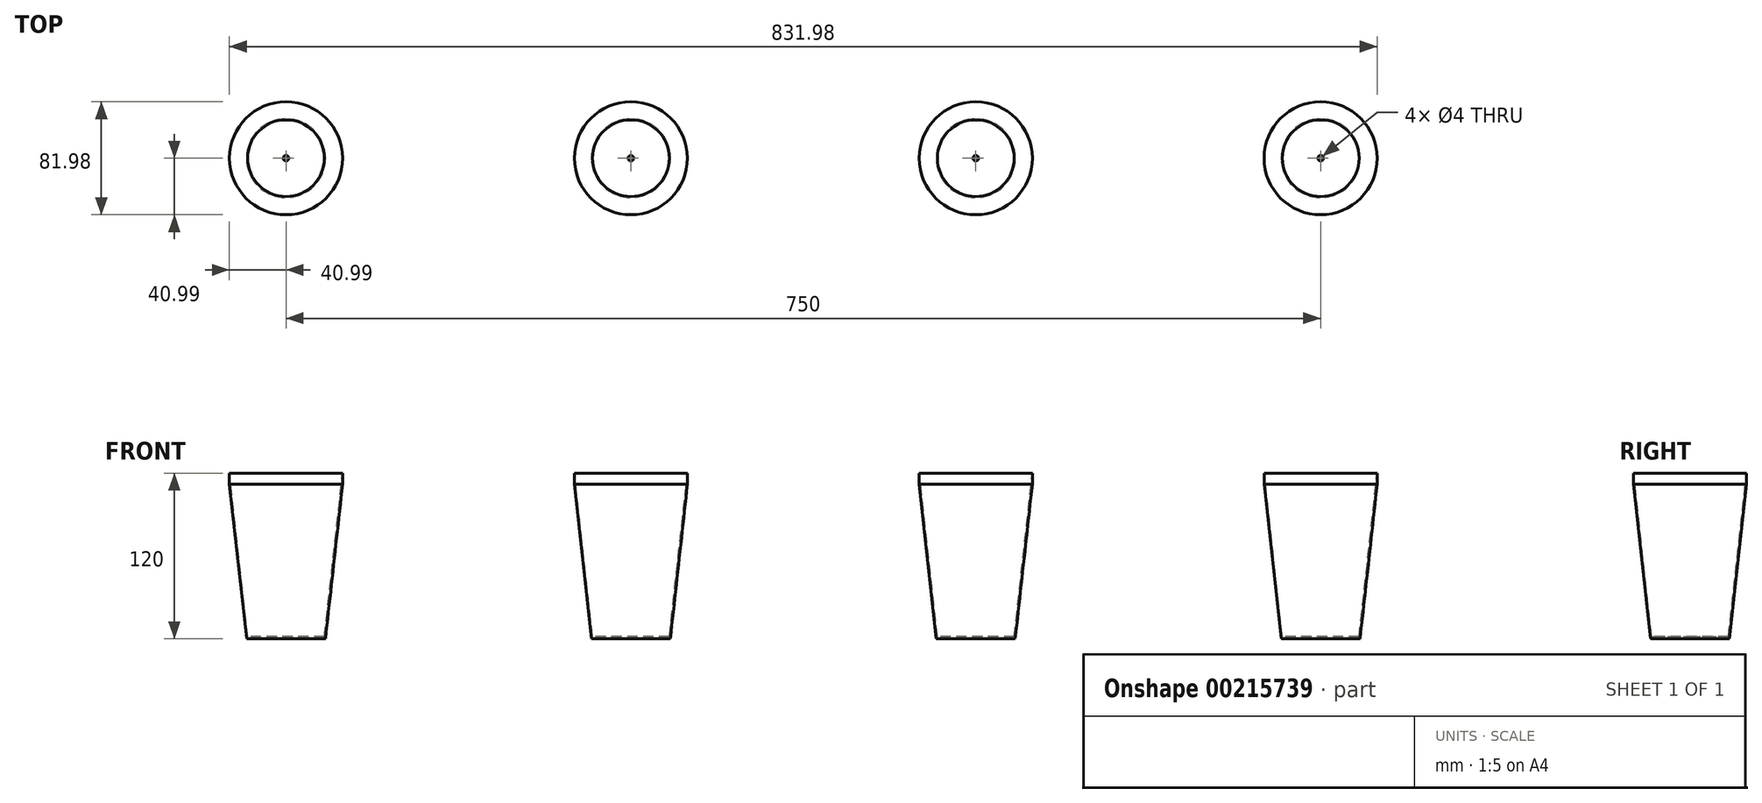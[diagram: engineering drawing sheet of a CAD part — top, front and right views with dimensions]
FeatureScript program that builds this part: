
annotation { "Feature Type Name" : "Feature", "Feature Type Description" : "" }
export const myFeature = defineFeature(function(context is Context, id is Id, definition is map)
    precondition{}
    {
        {
            var Q0;
            Q0=qCreatedBy(makeId("Front.planeOp"),FACE);
            var sketch = newSketch(context, id + "F0", { "sketchPlane" : qUnion([Q0])});
            skLineSegment(sketch, "E0", {"start": v(0, 0) * mm, "end": v(-28.58, 0) * mm});
            skLineSegment(sketch, "E1", {"start": v(-28.58, 0) * mm, "end": v(-40.99, 111.91) * mm});
            skLineSegment(sketch, "E2", {"start": v(-40.99, 111.91) * mm, "end": v(-40.99, 120) * mm});
            skLineSegment(sketch, "E3", {"start": v(-40.99, 120) * mm, "end": v(-27.85, 1.46) * mm});
            skLineSegment(sketch, "E4", {"start": v(-27.85, 1.46) * mm, "end": v(0, 1.46) * mm});
            skLineSegment(sketch, "E5", {"start": v(0, 1.46) * mm, "end": v(0, 0) * mm});
            skLineSegment(sketch, "E6", {"start": v(-2, 1.46) * mm, "end": v(-2, 0) * mm});
            skSolve(sketch);
        }
        {
            var Q0;
            {var subQ1=sQuery(id+"F0.wireOp",EDGE,"E1");Q0=makeQuery(id+"F0.imprint","IMPRINT",FACE,{"disambiguationData":[TD([[makeQuery(id+"F0.imprint","IMPRINT",EDGE,{"derivedFrom":subQ1}),-1.0]])]});}
            var Q1;
            Q1=sQuery(id+"F0.wireOp",EDGE,"E5");
            revolve(context, id + "F1", {"entities" : qUnion([Q0]), "axis" : qUnion([Q1]), "revolveType" : RevolveType.FULL});
        }
        {
            var Q0;
            Q0=qCreatedBy(makeId("Front.planeOp"),FACE);
            var sketch = newSketch(context, id + "F2", { "sketchPlane" : qUnion([Q0])});
            skLineSegment(sketch, "E7", {"start": v(250, 0) * mm, "end": v(221.42, 0) * mm});
            skLineSegment(sketch, "E8", {"start": v(221.42, 0) * mm, "end": v(209.01, 111.91) * mm});
            skLineSegment(sketch, "E9", {"start": v(209.01, 111.91) * mm, "end": v(209.01, 120) * mm});
            skLineSegment(sketch, "E10", {"start": v(209.01, 120) * mm, "end": v(222.15, 1.46) * mm});
            skLineSegment(sketch, "E11", {"start": v(222.15, 1.46) * mm, "end": v(250, 1.46) * mm});
            skLineSegment(sketch, "E12", {"start": v(250, 1.46) * mm, "end": v(250, 0) * mm});
            skLineSegment(sketch, "E13", {"start": v(248, 1.46) * mm, "end": v(248, 0) * mm});
            skSolve(sketch);
        }
        {
            var Q0;
            Q0=qCreatedBy(makeId("Front.planeOp"),FACE);
            var sketch = newSketch(context, id + "F3", { "sketchPlane" : qUnion([Q0])});
            skLineSegment(sketch, "E14", {"start": v(500, 0) * mm, "end": v(471.42, 0) * mm});
            skLineSegment(sketch, "E15", {"start": v(471.42, 0) * mm, "end": v(459.01, 111.91) * mm});
            skLineSegment(sketch, "E16", {"start": v(459.01, 111.91) * mm, "end": v(459.01, 120) * mm});
            skLineSegment(sketch, "E17", {"start": v(459.01, 120) * mm, "end": v(472.15, 1.46) * mm});
            skLineSegment(sketch, "E18", {"start": v(472.15, 1.46) * mm, "end": v(500, 1.46) * mm});
            skLineSegment(sketch, "E19", {"start": v(500, 1.46) * mm, "end": v(500, 0) * mm});
            skLineSegment(sketch, "E20", {"start": v(498, 1.46) * mm, "end": v(498, 0) * mm});
            skSolve(sketch);
        }
        {
            var Q0;
            {var subQ1=sQuery(id+"F2.wireOp",EDGE,"E8");Q0=makeQuery(id+"F2.imprint","IMPRINT",FACE,{"disambiguationData":[TD([[makeQuery(id+"F2.imprint","IMPRINT",EDGE,{"derivedFrom":subQ1}),-1.0]])]});}
            var Q1;
            Q1=sQuery(id+"F2.wireOp",EDGE,"E12");
            revolve(context, id + "F4", {"entities" : qUnion([Q0]), "axis" : qUnion([Q1]), "revolveType" : RevolveType.FULL});
        }
        {
            var Q0;
            {var subQ2=sQuery(id+"F3.wireOp",EDGE,"E15");Q0=makeQuery(id+"F3.imprint","IMPRINT",FACE,{"disambiguationData":[TD([[makeQuery(id+"F3.imprint","IMPRINT",EDGE,{"derivedFrom":subQ2}),-1.0]])]});}
            var Q1;
            Q1=sQuery(id+"F3.wireOp",EDGE,"E19");
            revolve(context, id + "F5", {"entities" : qUnion([Q0]), "axis" : qUnion([Q1]), "revolveType" : RevolveType.FULL});
        }
        {
            var Q0;
            Q0=qCreatedBy(makeId("Front.planeOp"),FACE);
            var sketch = newSketch(context, id + "F6", { "sketchPlane" : qUnion([Q0])});
            skLineSegment(sketch, "E21", {"start": v(750, 0) * mm, "end": v(721.42, 0) * mm});
            skLineSegment(sketch, "E22", {"start": v(721.42, 0) * mm, "end": v(709.01, 111.91) * mm});
            skLineSegment(sketch, "E23", {"start": v(709.01, 111.91) * mm, "end": v(709.01, 120) * mm});
            skLineSegment(sketch, "E24", {"start": v(709.01, 120) * mm, "end": v(722.15, 1.46) * mm});
            skLineSegment(sketch, "E25", {"start": v(722.15, 1.46) * mm, "end": v(750, 1.46) * mm});
            skLineSegment(sketch, "E26", {"start": v(750, 1.46) * mm, "end": v(750, 0) * mm});
            skLineSegment(sketch, "E27", {"start": v(748, 1.46) * mm, "end": v(748, 0) * mm});
            skSolve(sketch);
        }
        {
            var Q0;
            {var subQ1=sQuery(id+"F6.wireOp",EDGE,"E22");Q0=makeQuery(id+"F6.imprint","IMPRINT",FACE,{"disambiguationData":[TD([[makeQuery(id+"F6.imprint","IMPRINT",EDGE,{"derivedFrom":subQ1}),-1.0]])]});}
            var Q1;
            Q1=sQuery(id+"F6.wireOp",EDGE,"E26");
            revolve(context, id + "F7", {"entities" : qUnion([Q0]), "axis" : qUnion([Q1]), "revolveType" : RevolveType.FULL});
        }
    });
